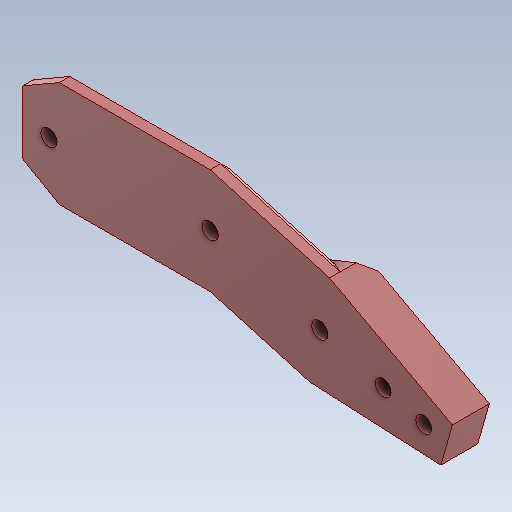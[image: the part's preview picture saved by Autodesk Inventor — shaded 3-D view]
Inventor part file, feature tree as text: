
AUTODESK INVENTOR PART (.ipt)
format: ipt  version: 2020 (Build 240168000, 168)  size: 222,208 bytes
history: native  units: in
note: dims shown in document units (in); Inventor stores cm internally (conversion verified against a paired STEP export)
features: extrude x3, sketch x3, projected_geometry x2, chamfer x1
ambient origin geometry x8: Origin, YZ Plane, XZ Plane, XY Plane, X Axis, Y Axis, Z Axis, Center Point
bodies: Solid1 (feature_tree)
feature tree (9):
  extrude  "Extrusion1"  Depth=1.2027in
  extrude  "Extrusion2"  Depth=1.1274in
  extrude  "Extrusion3"  Depth=0.0787in
  chamfer  "Chamfer1"  Distance=0.1969in
  sketch  "Sketch1"  dims[d0=0.122in d1=1.2027in]
  sketch  "Sketch3"  dims[d2=0.122in d3=1.1274in]
  projected_geometry  "Projected Loop2"
  sketch  "Sketch4"  dims[d4=0.122in d5=0.8503in d6=0.1969in d7=0.2362in d8=0.2362in d9=120.0deg d10=0.315in d11=120.0deg d12=0.315in d13=1.1268in d14=1.1268in d15=0.7744in d16=0.9262in d19=0.1575in d20=0.0in d23=0.0759in d54=0.9843in d55=180.0deg d56=0.1575in d57=0.1575in d58=90.0deg d59=90.0deg d60=0.1181in d61=0.315in d62=0.1181in d63=0.3937in d64=0.3937in d65=0.8933in d66=135.0deg d67=0.2756in d68=0.0in d69=0.2205in d70=0.2205in d71=0.2205in d72=0.0787in d73=0.0in d74=0.0787in d75=0.0787in d76=45.0deg]
  projected_geometry  "Projected Loop3"
